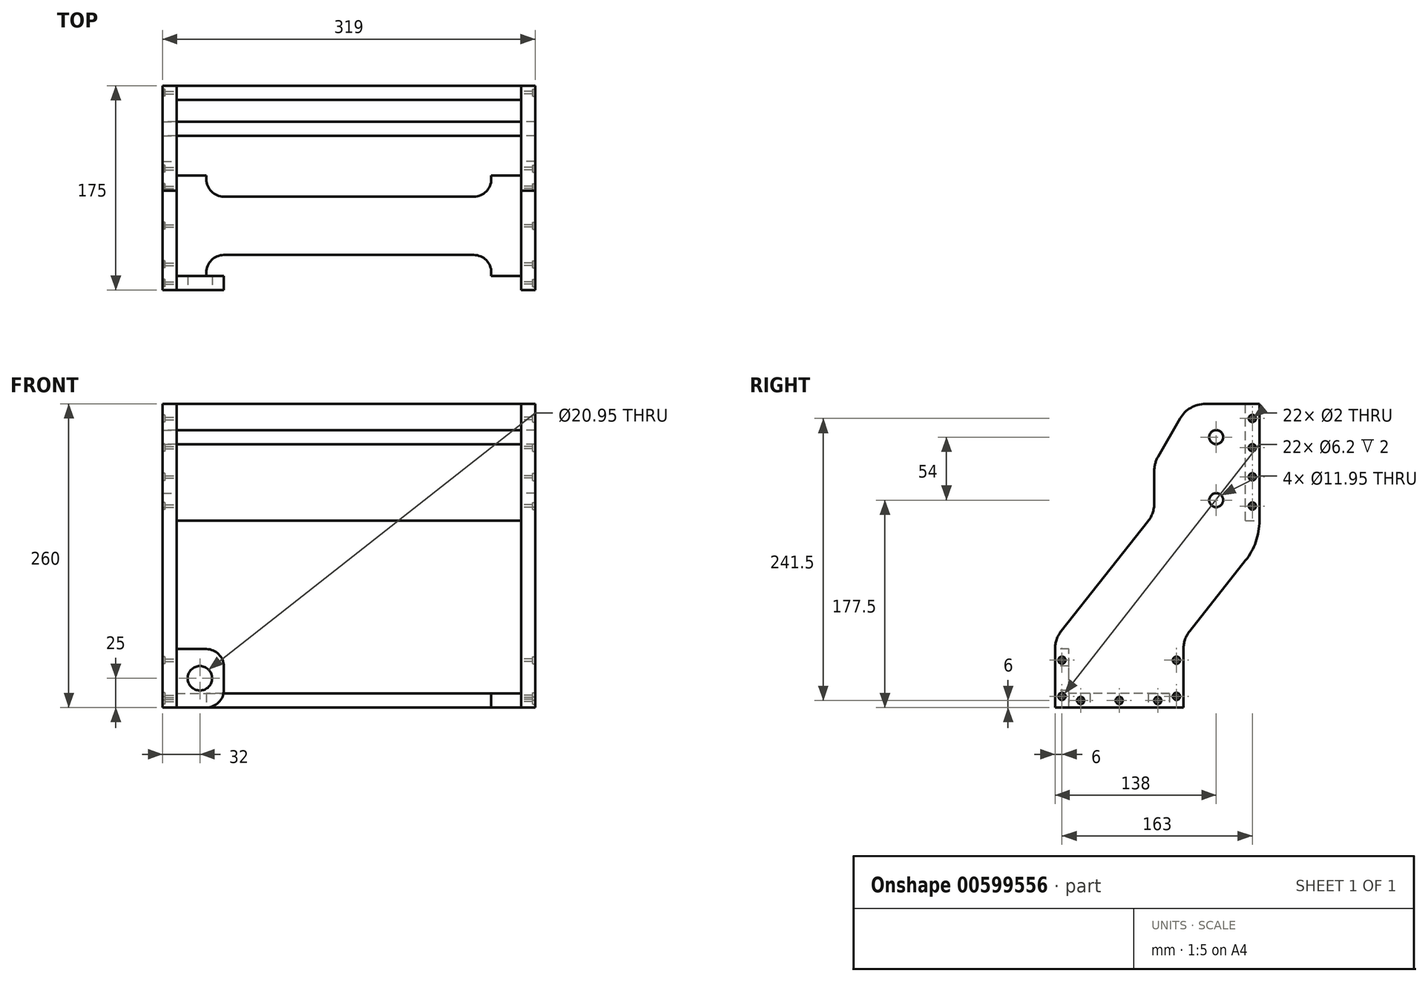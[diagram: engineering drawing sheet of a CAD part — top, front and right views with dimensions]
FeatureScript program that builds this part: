
annotation { "Feature Type Name" : "Feature", "Feature Type Description" : "" }
export const myFeature = defineFeature(function(context is Context, id is Id, definition is map)
    precondition{}
    {
        {
            var Q0;
            Q0=qCreatedBy(makeId("Front.planeOp"),FACE);
            var sketch = newSketch(context, id + "F0", { "sketchPlane" : qUnion([Q0])});
            skLineSegment(sketch, "E0.bottom", {"start": v(-147.5, 0) * mm, "end": v(147.5, 0) * mm});
            skLineSegment(sketch, "E0.top", {"start": v(-147.5, 100) * mm, "end": v(147.5, 100) * mm});
            skLineSegment(sketch, "E0.left", {"start": v(-147.5, 0) * mm, "end": v(-147.5, 100) * mm});
            skLineSegment(sketch, "E0.right", {"start": v(147.5, 0) * mm, "end": v(147.5, 100) * mm});
            skSolve(sketch);
        }
        {
            var Q0;
            Q0 = qSketchRegion(id + "F0", true);
            extrude(context, id + "F1", {"entities" : qUnion([Q0]), "depth" : 12 * mm, "offsetDistance" : 25 * mm});
        }
        {
            var Q0;
            Q0=makeQuery(id+"F1.opExtrude","SWEPT_FACE",FACE,{"disambiguationData":[OSD([sQuery(id+"F0.wireOp",EDGE,"E0.left")])]});
            var sketch = newSketch(context, id + "F2", { "sketchPlane" : qUnion([Q0])});
            skLineSegment(sketch, "E1.bottom", {"start": v(0, 100) * mm, "end": v(46.26, 100) * mm});
            skLineSegment(sketch, "E1.top", {"start": v(65, -160) * mm, "end": v(175, -160) * mm});
            skLineSegment(sketch, "E1.right", {"start": v(95.4, -0.65) * mm, "end": v(169.6, -94.5) * mm});
            skLineSegment(sketch, "E2", {"start": v(175, -160) * mm, "end": v(175, -110) * mm});
            skArc(sketch, "E3.filletArc", {"start": v(175, -110) * mm, "mid": v(173.61, -101.8) * mm, "end": v(169.6, -94.5) * mm});
            skLineSegment(sketch, "E4", {"start": v(11.86, -34.12) * mm, "end": v(59.6, -94.5) * mm});
            skLineSegment(sketch, "E5", {"start": v(0, 0) * mm, "end": v(0, 100) * mm});
            skArc(sketch, "E6.filletArc", {"start": v(0, 0) * mm, "mid": v(3.05, -18.06) * mm, "end": v(11.86, -34.12) * mm});
            skLineSegment(sketch, "E7", {"start": v(65, -160) * mm, "end": v(65, -110) * mm});
            skArc(sketch, "E8.filletArc", {"start": v(65, -110) * mm, "mid": v(63.61, -101.8) * mm, "end": v(59.6, -94.5) * mm});
            skLineSegment(sketch, "E9", {"start": v(90, 42.55) * mm, "end": v(90, 14.86) * mm});
            skArc(sketch, "E10.filletArc", {"start": v(90, 14.86) * mm, "mid": v(91.39, 6.65) * mm, "end": v(95.4, -0.65) * mm});
            skLineSegment(sketch, "E11", {"start": v(67.92, 87.5) * mm, "end": v(86.65, 55.05) * mm});
            skPoint(sketch, "E12.visualSharp", {"position": v(60.7, 100) * mm});
            skArc(sketch, "E12.filletArc", {"start": v(67.92, 87.5) * mm, "mid": v(58.76, 96.65) * mm, "end": v(46.26, 100) * mm});
            skArc(sketch, "E13.filletArc", {"start": v(90, 42.55) * mm, "mid": v(89.15, 49.02) * mm, "end": v(86.65, 55.05) * mm});
            skSolve(sketch);
        }
        {
            var Q0;
            Q0 = qSketchRegion(id + "F2", true);
            extrude(context, id + "F3", {"entities" : qUnion([Q0]), "depth" : 12 * mm, "offsetDistance" : 25 * mm});
        }
        {
            var Q0;
            Q0=makeQuery(id+"F3.opExtrude","CAP_FACE",FACE,{"disambiguationData":[OSD([sQuery(id+"F2.wireOp",EDGE,"E1.bottom"),sQuery(id+"F2.wireOp",EDGE,"E1.top"),sQuery(id+"F2.wireOp",EDGE,"E1.left"),sQuery(id+"F2.wireOp",EDGE,"E1.right"),sQuery(id+"F2.wireOp",EDGE,"E2"),sQuery(id+"F2.wireOp",EDGE,"2146645f-f5f1-4766-9391-dd441536dbd0.filletArc"),sQuery(id+"F2.wireOp",EDGE,"E3.filletArc")])],"isStart":true});
            var sketch = newSketch(context, id + "F4", { "sketchPlane" : qUnion([Q0])});
            skCircle(sketch, "E14", {"center": v(-37, 17.5) * mm, "radius": 5.97 * mm});
            skCircle(sketch, "E15", {"center": v(-37, 71.5) * mm, "radius": 5.97 * mm});
            skLineSegment(sketch, "E16", {"start": v(-37, 17.5) * mm, "end": v(-37, 71.5) * mm, "construction": true});
            skCircle(sketch, "E17", {"center": v(-6, 87.5) * mm, "radius": 1 * mm});
            skCircle(sketch, "E18.0.1.0", {"center": v(-6, 62.5) * mm, "radius": 1 * mm});
            skCircle(sketch, "E18.0.2.0", {"center": v(-6, 37.5) * mm, "radius": 1 * mm});
            skCircle(sketch, "E18.0.3.0", {"center": v(-6, 12.5) * mm, "radius": 1 * mm});
            skLineSegment(sketch, "E18.direction1", {"start": v(-6, 87.5) * mm, "end": v(0, 87.5) * mm, "construction": true});
            skLineSegment(sketch, "E18.direction2", {"start": v(-6, 87.5) * mm, "end": v(-6, 62.5) * mm, "construction": true});
            skCircle(sketch, "E19", {"center": v(-87, -154) * mm, "radius": 1 * mm});
            skCircle(sketch, "E20.1.0.0", {"center": v(-120, -154) * mm, "radius": 1 * mm});
            skCircle(sketch, "E20.2.0.0", {"center": v(-153, -154) * mm, "radius": 1 * mm});
            skLineSegment(sketch, "E20.direction1", {"start": v(-87, -154) * mm, "end": v(-120, -154) * mm, "construction": true});
            skLineSegment(sketch, "E21", {"start": v(-120, -154) * mm, "end": v(-120, -160) * mm, "construction": true});
            skCircle(sketch, "E22", {"center": v(-169, -150.5) * mm, "radius": 1 * mm});
            skCircle(sketch, "E23", {"center": v(-169, -119.5) * mm, "radius": 1 * mm});
            skLineSegment(sketch, "E24", {"start": v(-169, -119.5) * mm, "end": v(-169, -150.5) * mm, "construction": true});
            skCircle(sketch, "E25.MirrorC", {"center": v(-71, -119.5) * mm, "radius": 1 * mm});
            skCircle(sketch, "E26.MirrorC", {"center": v(-71, -150.5) * mm, "radius": 1 * mm});
            skSolve(sketch);
        }
        {
            var Q0;
            Q0 = qSketchRegion(id + "F4", true);
            extrude(context, id + "F5", {"entities" : qUnion([Q0]), "operationType" : NewBodyOperationType.REMOVE, "oppositeDirection" : true, "depth" : 25 * mm, "offsetDistance" : 25 * mm});
        }
        {
            var Q0;
            Q0=makeQuery(id+"F3.opExtrude","CAP_FACE",FACE,{"disambiguationData":[OSD([sQuery(id+"F2.wireOp",EDGE,"E1.bottom"),sQuery(id+"F2.wireOp",EDGE,"E1.top"),sQuery(id+"F2.wireOp",EDGE,"E1.left"),sQuery(id+"F2.wireOp",EDGE,"E1.right"),sQuery(id+"F2.wireOp",EDGE,"E2"),sQuery(id+"F2.wireOp",EDGE,"2146645f-f5f1-4766-9391-dd441536dbd0.filletArc"),sQuery(id+"F2.wireOp",EDGE,"E3.filletArc")])],"isStart":false});
            var sketch = newSketch(context, id + "F6", { "sketchPlane" : qUnion([Q0])});
            skCircle(sketch, "E27", {"center": v(37, 71.5) * mm, "radius": 6 * mm});
            skSolve(sketch);
        }
        {
            var Q0;
            Q0 = qSketchRegion(id + "F6", true);
            extrude(context, id + "F7", {"entities" : qUnion([Q0]), "oppositeDirection" : true, "depth" : 319 * mm, "offsetDistance" : 25 * mm});
        }
        {
            var Q0;
            Q0=makeQuery(id+"F1.opExtrude","SWEPT_FACE",FACE,{"disambiguationData":[OSD([sQuery(id+"F0.wireOp",EDGE,"E0.right")])]});
            var sketch = newSketch(context, id + "F8", { "sketchPlane" : qUnion([Q0])});
            skCircle(sketch, "E28.0", {"center": v(-37, 71.5) * mm, "radius": 5.97 * mm});
            skCircle(sketch, "E29.0", {"center": v(-37, 17.5) * mm, "radius": 5.97 * mm});
            skCircle(sketch, "E30.0", {"center": v(-6, 12.5) * mm, "radius": 1 * mm});
            skArc(sketch, "E31.0", {"start": v(-11.86, -34.12) * mm, "mid": v(-3.05, -18.06) * mm, "end": v(0, 0) * mm});
            skLineSegment(sketch, "E31.1", {"start": v(-59.6, -94.5) * mm, "end": v(-11.86, -34.12) * mm});
            skArc(sketch, "E31.2", {"start": v(-90, 14.86) * mm, "mid": v(-91.39, 6.65) * mm, "end": v(-95.4, -0.65) * mm});
            skLineSegment(sketch, "E31.3", {"start": v(-90, 42.55) * mm, "end": v(-90, 14.86) * mm});
            skLineSegment(sketch, "E31.5", {"start": v(0, 100) * mm, "end": v(-46.26, 100) * mm});
            skLineSegment(sketch, "E31.6", {"start": v(-95.4, -0.65) * mm, "end": v(-169.6, -94.5) * mm});
            skArc(sketch, "E31.7", {"start": v(-169.6, -94.5) * mm, "mid": v(-173.61, -101.8) * mm, "end": v(-175, -110) * mm});
            skLineSegment(sketch, "E31.8", {"start": v(0, 0) * mm, "end": v(0, 100) * mm});
            skLineSegment(sketch, "E31.9", {"start": v(-175, -110) * mm, "end": v(-175, -160) * mm});
            skLineSegment(sketch, "E31.10", {"start": v(-175, -160) * mm, "end": v(-65, -160) * mm});
            skLineSegment(sketch, "E31.11", {"start": v(-65, -160) * mm, "end": v(-65, -110) * mm});
            skArc(sketch, "E31.12", {"start": v(-65, -110) * mm, "mid": v(-63.61, -101.8) * mm, "end": v(-59.6, -94.5) * mm});
            skCircle(sketch, "E32.0", {"center": v(-6, 37.5) * mm, "radius": 1 * mm});
            skCircle(sketch, "E33.0", {"center": v(-6, 62.5) * mm, "radius": 1 * mm});
            skCircle(sketch, "E34.0", {"center": v(-6, 87.5) * mm, "radius": 1 * mm});
            skArc(sketch, "E35.0", {"start": v(-67.92, 87.5) * mm, "mid": v(-58.76, 96.65) * mm, "end": v(-46.26, 100) * mm});
            skLineSegment(sketch, "E35.1", {"start": v(-67.92, 87.5) * mm, "end": v(-86.65, 55.05) * mm});
            skArc(sketch, "E35.2", {"start": v(-90, 42.55) * mm, "mid": v(-89.15, 49.02) * mm, "end": v(-86.65, 55.05) * mm});
            skCircle(sketch, "E36.0", {"center": v(-153, -154) * mm, "radius": 1 * mm});
            skCircle(sketch, "E37.0", {"center": v(-120, -154) * mm, "radius": 1 * mm});
            skCircle(sketch, "E38.0", {"center": v(-87, -154) * mm, "radius": 1 * mm});
            skCircle(sketch, "E39.0", {"center": v(-169, -150.5) * mm, "radius": 1 * mm});
            skCircle(sketch, "E40.0", {"center": v(-169, -119.5) * mm, "radius": 1 * mm});
            skCircle(sketch, "E41.0", {"center": v(-71, -150.5) * mm, "radius": 1 * mm});
            skCircle(sketch, "E42.0", {"center": v(-71, -119.5) * mm, "radius": 1 * mm});
            skSolve(sketch);
        }
        {
            var Q0;
            Q0 = qSketchRegion(id + "F8", true);
            extrude(context, id + "F9", {"entities" : qUnion([Q0]), "depth" : 12 * mm, "offsetDistance" : 25 * mm});
        }
        {
            var Q0;
            Q0=makeQuery(id+"F3.opExtrude","CAP_FACE",FACE,{"disambiguationData":[OSD([sQuery(id+"F2.wireOp",EDGE,"E1.bottom"),sQuery(id+"F2.wireOp",EDGE,"E1.top"),sQuery(id+"F2.wireOp",EDGE,"E1.left"),sQuery(id+"F2.wireOp",EDGE,"E1.right"),sQuery(id+"F2.wireOp",EDGE,"E2"),sQuery(id+"F2.wireOp",EDGE,"2146645f-f5f1-4766-9391-dd441536dbd0.filletArc"),sQuery(id+"F2.wireOp",EDGE,"E3.filletArc")])],"isStart":false});
            var sketch = newSketch(context, id + "F10", { "sketchPlane" : qUnion([Q0])});
            skCircle(sketch, "E43", {"center": v(6, 87.5) * mm, "radius": 3.1 * mm});
            skCircle(sketch, "E44.0.1.0", {"center": v(6, 62.5) * mm, "radius": 3.1 * mm});
            skCircle(sketch, "E44.0.2.0", {"center": v(6, 37.5) * mm, "radius": 3.1 * mm});
            skCircle(sketch, "E44.0.3.0", {"center": v(6, 12.5) * mm, "radius": 3.1 * mm});
            skLineSegment(sketch, "E44.direction1", {"start": v(6, 87.5) * mm, "end": v(31, 87.5) * mm, "construction": true});
            skLineSegment(sketch, "E44.direction2", {"start": v(6, 87.5) * mm, "end": v(6, 62.5) * mm, "construction": true});
            skCircle(sketch, "E45.0", {"center": v(87, -154) * mm, "radius": 3.1 * mm});
            skCircle(sketch, "E46.0", {"center": v(120, -154) * mm, "radius": 3.1 * mm});
            skCircle(sketch, "E47.0", {"center": v(153, -154) * mm, "radius": 3.1 * mm});
            skCircle(sketch, "E48", {"center": v(71, -150.5) * mm, "radius": 3.1 * mm});
            skCircle(sketch, "E49", {"center": v(71, -119.5) * mm, "radius": 3.1 * mm});
            skCircle(sketch, "E50", {"center": v(169, -119.5) * mm, "radius": 3.1 * mm});
            skCircle(sketch, "E51", {"center": v(169, -150.5) * mm, "radius": 3.1 * mm});
            skSolve(sketch);
        }
        {
            var Q0;
            Q0 = qSketchRegion(id + "F10", true);
            extrude(context, id + "F11", {"entities" : qUnion([Q0]), "operationType" : NewBodyOperationType.REMOVE, "oppositeDirection" : true, "depth" : 2 * mm, "offsetDistance" : 25 * mm});
        }
        {
            var Q0;
            Q0=makeQuery(id+"F9.opExtrude","CAP_FACE",FACE,{"disambiguationData":[OSD([sQuery(id+"F8.wireOp",EDGE,"bbb40a25-6dec-4c05-81ac-04070c8977a2.0"),sQuery(id+"F8.wireOp",EDGE,"bbb40a25-6dec-4c05-81ac-04070c8977a2.1"),sQuery(id+"F8.wireOp",EDGE,"bbb40a25-6dec-4c05-81ac-04070c8977a2.2"),sQuery(id+"F8.wireOp",EDGE,"bbb40a25-6dec-4c05-81ac-04070c8977a2.3"),sQuery(id+"F8.wireOp",EDGE,"bbb40a25-6dec-4c05-81ac-04070c8977a2.4"),sQuery(id+"F8.wireOp",EDGE,"bbb40a25-6dec-4c05-81ac-04070c8977a2.5"),sQuery(id+"F8.wireOp",EDGE,"bbb40a25-6dec-4c05-81ac-04070c8977a2.6"),sQuery(id+"F8.wireOp",EDGE,"E28.0"),sQuery(id+"F8.wireOp",EDGE,"E29.0"),sQuery(id+"F8.wireOp",EDGE,"6efdfc97-257b-474c-8056-4d0e825cf1ba.0"),sQuery(id+"F8.wireOp",EDGE,"a72bb776-54a7-4bf9-87ab-a64d75e5a3ff.0"),sQuery(id+"F8.wireOp",EDGE,"8cdf7bf5-7813-4b78-9d66-bfd1ffc78f39.0"),sQuery(id+"F8.wireOp",EDGE,"E30.0")])],"isStart":false});
            var sketch = newSketch(context, id + "F12", { "sketchPlane" : qUnion([Q0])});
            skCircle(sketch, "E52", {"center": v(-6, 87.5) * mm, "radius": 3.1 * mm});
            skCircle(sketch, "E53.0.1.0", {"center": v(-6, 62.5) * mm, "radius": 3.1 * mm});
            skCircle(sketch, "E53.0.2.0", {"center": v(-6, 37.5) * mm, "radius": 3.1 * mm});
            skCircle(sketch, "E53.0.3.0", {"center": v(-6, 12.5) * mm, "radius": 3.1 * mm});
            skLineSegment(sketch, "E53.direction1", {"start": v(-6, 87.5) * mm, "end": v(19, 87.5) * mm, "construction": true});
            skLineSegment(sketch, "E53.direction2", {"start": v(-6, 87.5) * mm, "end": v(-6, 62.5) * mm, "construction": true});
            skCircle(sketch, "E54.0", {"center": v(-153, -154) * mm, "radius": 3.1 * mm});
            skCircle(sketch, "E55.0", {"center": v(-120, -154) * mm, "radius": 3.1 * mm});
            skCircle(sketch, "E56.0", {"center": v(-87, -154) * mm, "radius": 3.1 * mm});
            skCircle(sketch, "E57", {"center": v(-71, -150.5) * mm, "radius": 3.1 * mm});
            skCircle(sketch, "E58", {"center": v(-71, -119.5) * mm, "radius": 3.1 * mm});
            skCircle(sketch, "E59", {"center": v(-169, -150.5) * mm, "radius": 3.1 * mm});
            skCircle(sketch, "E60", {"center": v(-169, -119.5) * mm, "radius": 3.1 * mm});
            skSolve(sketch);
        }
        {
            var Q0;
            Q0 = qSketchRegion(id + "F12", true);
            extrude(context, id + "F13", {"entities" : qUnion([Q0]), "operationType" : NewBodyOperationType.REMOVE, "oppositeDirection" : true, "depth" : 2 * mm, "offsetDistance" : 25 * mm});
        }
        {
            var Q0;
            Q0=makeQuery(id+"F3.opExtrude","SWEPT_FACE",FACE,{"disambiguationData":[OSD([sQuery(id+"F2.wireOp",EDGE,"E2")])]});
            var sketch = newSketch(context, id + "F14", { "sketchPlane" : qUnion([Q0])});
            skLineSegment(sketch, "E61.bottom", {"start": v(-147.5, -160) * mm, "end": v(-122, -160) * mm});
            skLineSegment(sketch, "E61.top", {"start": v(-147.5, -110) * mm, "end": v(-122, -110) * mm});
            skLineSegment(sketch, "E61.left", {"start": v(-147.5, -160) * mm, "end": v(-147.5, -110) * mm});
            skLineSegment(sketch, "E61.right", {"start": v(-107, -145) * mm, "end": v(-107, -125) * mm});
            skCircle(sketch, "E62", {"center": v(-127.5, -135) * mm, "radius": 10.47 * mm});
            skPoint(sketch, "E62.centerSnap0", {"position": v(-147.5, -135) * mm});
            skPoint(sketch, "E62.centerSnap1", {"position": v(-127.5, -160) * mm});
            skArc(sketch, "E63.filletArc", {"start": v(-107, -125) * mm, "mid": v(-111.4, -114.4) * mm, "end": v(-122, -110) * mm});
            skArc(sketch, "E64.filletArc", {"start": v(-122, -160) * mm, "mid": v(-111.4, -155.6) * mm, "end": v(-107, -145) * mm});
            skSolve(sketch);
        }
        {
            var Q0;
            Q0 = qSketchRegion(id + "F14", true);
            extrude(context, id + "F15", {"entities" : qUnion([Q0]), "oppositeDirection" : true, "depth" : 12 * mm, "offsetDistance" : 25 * mm});
        }
        {
            var Q0;
            Q0=makeQuery(id+"F3.opExtrude","SWEPT_FACE",FACE,{"disambiguationData":[OSD([sQuery(id+"F2.wireOp",EDGE,"E1.top")])]});
            var sketch = newSketch(context, id + "F16", { "sketchPlane" : qUnion([Q0])});
            skLineSegment(sketch, "E65.bottom", {"start": v(-107, 145) * mm, "end": v(0, 145) * mm});
            skLineSegment(sketch, "E65.top", {"start": v(-147.5, 120) * mm, "end": v(147.5, 120) * mm, "construction": true});
            skLineSegment(sketch, "E66.top", {"start": v(-147.5, 163) * mm, "end": v(-122, 163) * mm});
            skPoint(sketch, "E67", {"position": v(-147.5, 120) * mm});
            skLineSegment(sketch, "E68.trimOffspring", {"start": v(-122, 160) * mm, "end": v(-122, 163) * mm});
            skPoint(sketch, "E69.visualSharp", {"position": v(-122, 145) * mm});
            skArc(sketch, "E69.filletArc", {"start": v(-122, 160) * mm, "mid": v(-117.6, 149.4) * mm, "end": v(-107, 145) * mm});
            skLineSegment(sketch, "E70", {"start": v(-147.5, 163) * mm, "end": v(-147.5, 120) * mm});
            skLineSegment(sketch, "E71", {"start": v(0, 120) * mm, "end": v(0, 145) * mm, "construction": true});
            skLineSegment(sketch, "E72.MirrorCS", {"start": v(107, 145) * mm, "end": v(0, 145) * mm});
            skArc(sketch, "E73.MirrorCS", {"start": v(122, 160) * mm, "mid": v(117.6, 149.4) * mm, "end": v(107, 145) * mm});
            skLineSegment(sketch, "E74.MirrorCS", {"start": v(122, 160) * mm, "end": v(122, 163) * mm});
            skLineSegment(sketch, "E75.MirrorCS", {"start": v(147.5, 163) * mm, "end": v(122, 163) * mm});
            skLineSegment(sketch, "E76.MirrorCS", {"start": v(147.5, 163) * mm, "end": v(147.5, 120) * mm});
            skLineSegment(sketch, "E77.MirrorCS", {"start": v(-122, 80) * mm, "end": v(-122, 77) * mm});
            skLineSegment(sketch, "E78.MirrorCS", {"start": v(122, 80) * mm, "end": v(122, 77) * mm});
            skLineSegment(sketch, "E79.MirrorCS", {"start": v(-147.5, 77) * mm, "end": v(-122, 77) * mm});
            skLineSegment(sketch, "E80.MirrorCS", {"start": v(147.5, 77) * mm, "end": v(122, 77) * mm});
            skLineSegment(sketch, "E81.MirrorCS", {"start": v(147.5, 77) * mm, "end": v(147.5, 120) * mm});
            skLineSegment(sketch, "E82.MirrorCS", {"start": v(-107, 95) * mm, "end": v(0, 95) * mm});
            skArc(sketch, "E83.MirrorCS", {"start": v(122, 80) * mm, "mid": v(117.6, 90.6) * mm, "end": v(107, 95) * mm});
            skLineSegment(sketch, "E84.MirrorCS", {"start": v(107, 95) * mm, "end": v(0, 95) * mm});
            skPoint(sketch, "E85.MirrorP", {"position": v(-122, 95) * mm});
            skArc(sketch, "E86.MirrorCS", {"start": v(-122, 80) * mm, "mid": v(-117.6, 90.6) * mm, "end": v(-107, 95) * mm});
            skLineSegment(sketch, "E87.MirrorCS", {"start": v(-147.5, 77) * mm, "end": v(-147.5, 120) * mm});
            skSolve(sketch);
        }
        {
            var Q0;
            Q0 = qSketchRegion(id + "F16", true);
            extrude(context, id + "F17", {"entities" : qUnion([Q0]), "oppositeDirection" : true, "depth" : 12 * mm, "offsetDistance" : 25 * mm});
        }
    });
